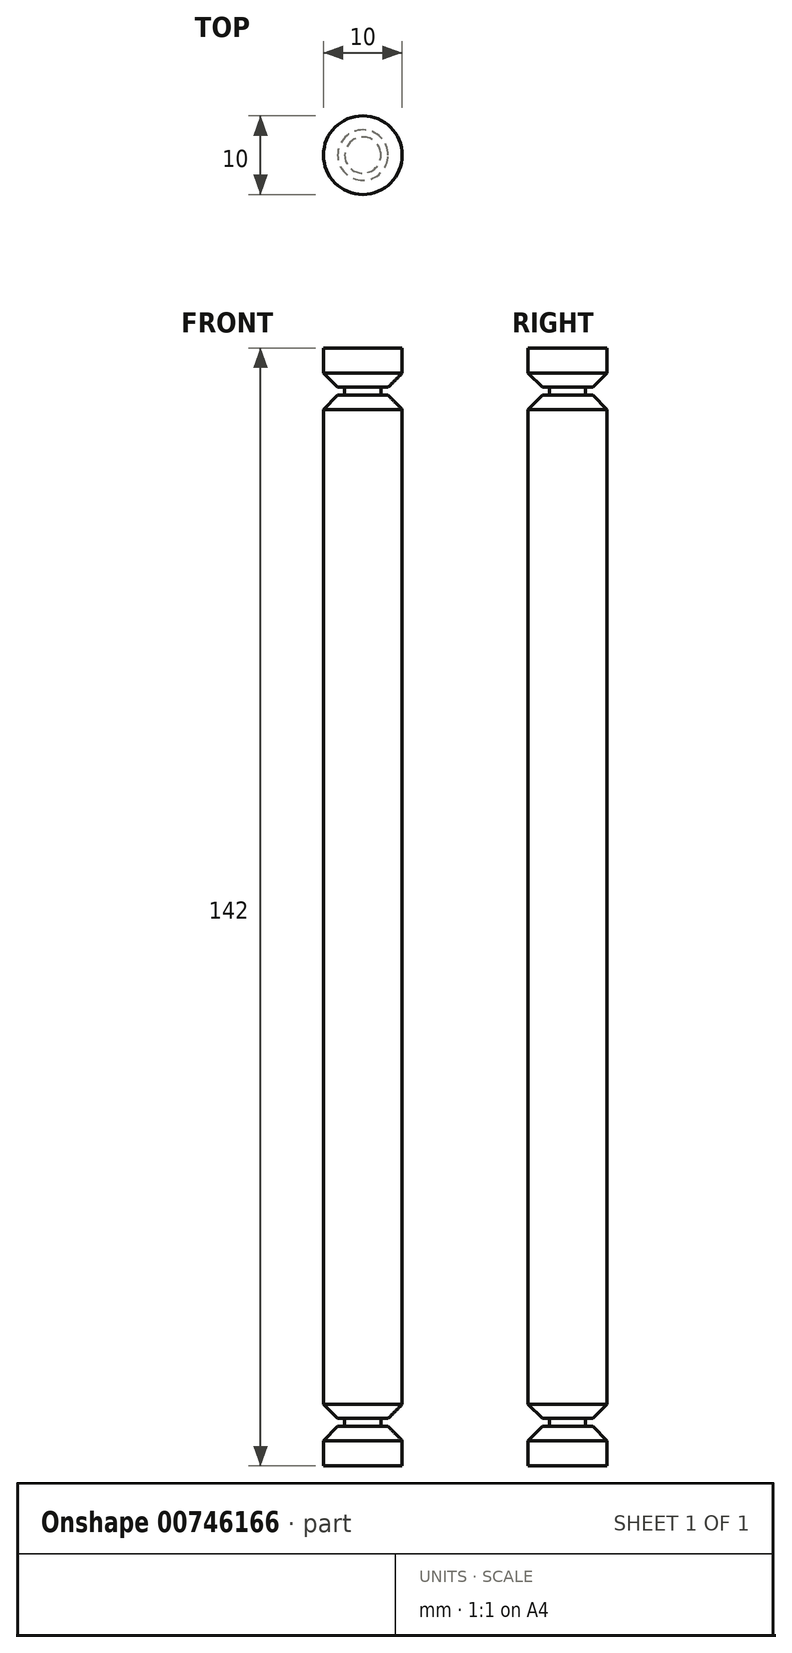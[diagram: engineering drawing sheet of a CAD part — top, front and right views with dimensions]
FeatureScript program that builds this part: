
annotation { "Feature Type Name" : "Feature", "Feature Type Description" : "" }
export const myFeature = defineFeature(function(context is Context, id is Id, definition is map)
    precondition{}
    {
        {
            var Q0;
            Q0=qCreatedBy(makeId("Top.planeOp"),FACE);
            var sketch = newSketch(context, id + "F0", { "sketchPlane" : qUnion([Q0])});
            skCircle(sketch, "E0", {"center": v(0, 0) * mm, "radius": 5 * mm});
            skCircle(sketch, "E1", {"center": v(0, 0) * mm, "radius": 2.3 * mm});
            skSolve(sketch);
        }
        {
            var Q0;
            Q0=makeQuery(id+"F0.imprint","IMPRINT",FACE,{"disambiguationData":[TD([[makeQuery(id+"F0.imprint","IMPRINT",EDGE,{"derivedFrom":sQuery(id+"F0.wireOp",EDGE,"E0")}),1.0]])]});
            var Q1;
            Q1=makeQuery(id+"F0.imprint","IMPRINT",FACE,{"disambiguationData":[TD([[makeQuery(id+"F0.imprint","IMPRINT",EDGE,{"derivedFrom":sQuery(id+"F0.wireOp",EDGE,"E1")}),1.0]])]});
            extrude(context, id + "F1", {"entities" : qUnion([Q0, Q1]), "depth" : 5 * mm, "offsetDistance" : 25 * mm});
        }
        {
            var Q0;
            Q0=makeQuery(id+"F0.imprint","IMPRINT",FACE,{"disambiguationData":[TD([[makeQuery(id+"F0.imprint","IMPRINT",EDGE,{"derivedFrom":sQuery(id+"F0.wireOp",EDGE,"E1")}),1.0]])]});
            var Q1;
            Q1=makeQuery(id+"F1.opExtrude","CAP_FACE",FACE,{"disambiguationData":[OSD([sQuery(id+"F0.wireOp",EDGE,"E0")])],"isStart":false});
            extrude(context, id + "F2", {"entities" : qUnion([Q0]), "operationType" : NewBodyOperationType.ADD, "depth" : 6 * mm, "offsetDistance" : 25 * mm, "hasSecondDirection" : true, "secondDirectionBound" : SecondDirectionBoundingType.UP_TO_SURFACE, "secondDirectionOppositeDirection" : false, "secondDirectionDepth" : 4.8 * mm, "secondDirectionBoundEntityFace" : qUnion([Q1])});
        }
        {
            var Q0;
            Q0=makeQuery(id+"F0.imprint","IMPRINT",FACE,{"disambiguationData":[TD([[makeQuery(id+"F0.imprint","IMPRINT",EDGE,{"derivedFrom":sQuery(id+"F0.wireOp",EDGE,"E1")}),1.0]])]});
            var Q1;
            Q1=makeQuery(id+"F0.imprint","IMPRINT",FACE,{"disambiguationData":[TD([[makeQuery(id+"F0.imprint","IMPRINT",EDGE,{"derivedFrom":sQuery(id+"F0.wireOp",EDGE,"E0")}),1.0]])]});
            var Q2;
            Q2=makeQuery(id+"F2.opExtrude","CAP_FACE",FACE,{"disambiguationData":[OSD([sQuery(id+"F0.wireOp",EDGE,"E1")])],"isStart":false});
            extrude(context, id + "F3", {"entities" : qUnion([Q0, Q1]), "operationType" : NewBodyOperationType.ADD, "depth" : 136 * mm, "offsetDistance" : 25 * mm, "hasSecondDirection" : true, "secondDirectionBound" : SecondDirectionBoundingType.UP_TO_SURFACE, "secondDirectionOppositeDirection" : false, "secondDirectionDepth" : 8.4 * mm, "secondDirectionBoundEntityFace" : qUnion([Q2])});
        }
        {
            var Q0;
            Q0=makeQuery(id+"F0.imprint","IMPRINT",FACE,{"disambiguationData":[TD([[makeQuery(id+"F0.imprint","IMPRINT",EDGE,{"derivedFrom":sQuery(id+"F0.wireOp",EDGE,"E1")}),1.0]])]});
            var Q1;
            Q1=makeQuery(id+"F3.opExtrude","CAP_FACE",FACE,{"disambiguationData":[OSD([sQuery(id+"F0.wireOp",EDGE,"E0")])],"isStart":false});
            extrude(context, id + "F4", {"entities" : qUnion([Q0]), "operationType" : NewBodyOperationType.ADD, "depth" : 137 * mm, "offsetDistance" : 25 * mm, "hasSecondDirection" : true, "secondDirectionBound" : SecondDirectionBoundingType.UP_TO_SURFACE, "secondDirectionOppositeDirection" : false, "secondDirectionDepth" : 132 * mm, "secondDirectionBoundEntityFace" : qUnion([Q1])});
        }
        {
            var Q0;
            Q0=makeQuery(id+"F0.imprint","IMPRINT",FACE,{"disambiguationData":[TD([[makeQuery(id+"F0.imprint","IMPRINT",EDGE,{"derivedFrom":sQuery(id+"F0.wireOp",EDGE,"E1")}),1.0]])]});
            var Q1;
            Q1=makeQuery(id+"F0.imprint","IMPRINT",FACE,{"disambiguationData":[TD([[makeQuery(id+"F0.imprint","IMPRINT",EDGE,{"derivedFrom":sQuery(id+"F0.wireOp",EDGE,"E0")}),1.0]])]});
            var Q2;
            Q2=makeQuery(id+"F4.opExtrude","CAP_FACE",FACE,{"disambiguationData":[OSD([sQuery(id+"F0.wireOp",EDGE,"E1")])],"isStart":false});
            extrude(context, id + "F5", {"entities" : qUnion([Q0, Q1]), "operationType" : NewBodyOperationType.ADD, "depth" : 142 * mm, "offsetDistance" : 25 * mm, "hasSecondDirection" : true, "secondDirectionBound" : SecondDirectionBoundingType.UP_TO_SURFACE, "secondDirectionOppositeDirection" : false, "secondDirectionDepth" : 25 * mm, "secondDirectionBoundEntityFace" : qUnion([Q2])});
        }
        {
            var Q0;
            Q0=makeQuery(id+"F3.opExtrude","CAP_EDGE",EDGE,{"disambiguationData":[OSD([sQuery(id+"F0.wireOp",EDGE,"E0")])],"isStart":false});
            var Q1;
            Q1=makeQuery(id+"F5.opExtrude","CAP_EDGE",EDGE,{"disambiguationData":[OSD([sQuery(id+"F0.wireOp",EDGE,"E0")])],"isStart":true});
            var Q2;
            Q2=makeQuery(id+"F3.opExtrude","CAP_EDGE",EDGE,{"disambiguationData":[OSD([sQuery(id+"F0.wireOp",EDGE,"E0")])],"isStart":true});
            var Q3;
            Q3=makeQuery(id+"F1.opExtrude","CAP_EDGE",EDGE,{"disambiguationData":[OSD([sQuery(id+"F0.wireOp",EDGE,"E0")])],"isStart":false});
            chamfer(context, id + "F6", {"entities" : qUnion([Q0, Q1, Q2, Q3]), "width" : 1.8 * mm, "tangentPropagation" : true});
        }
    });
